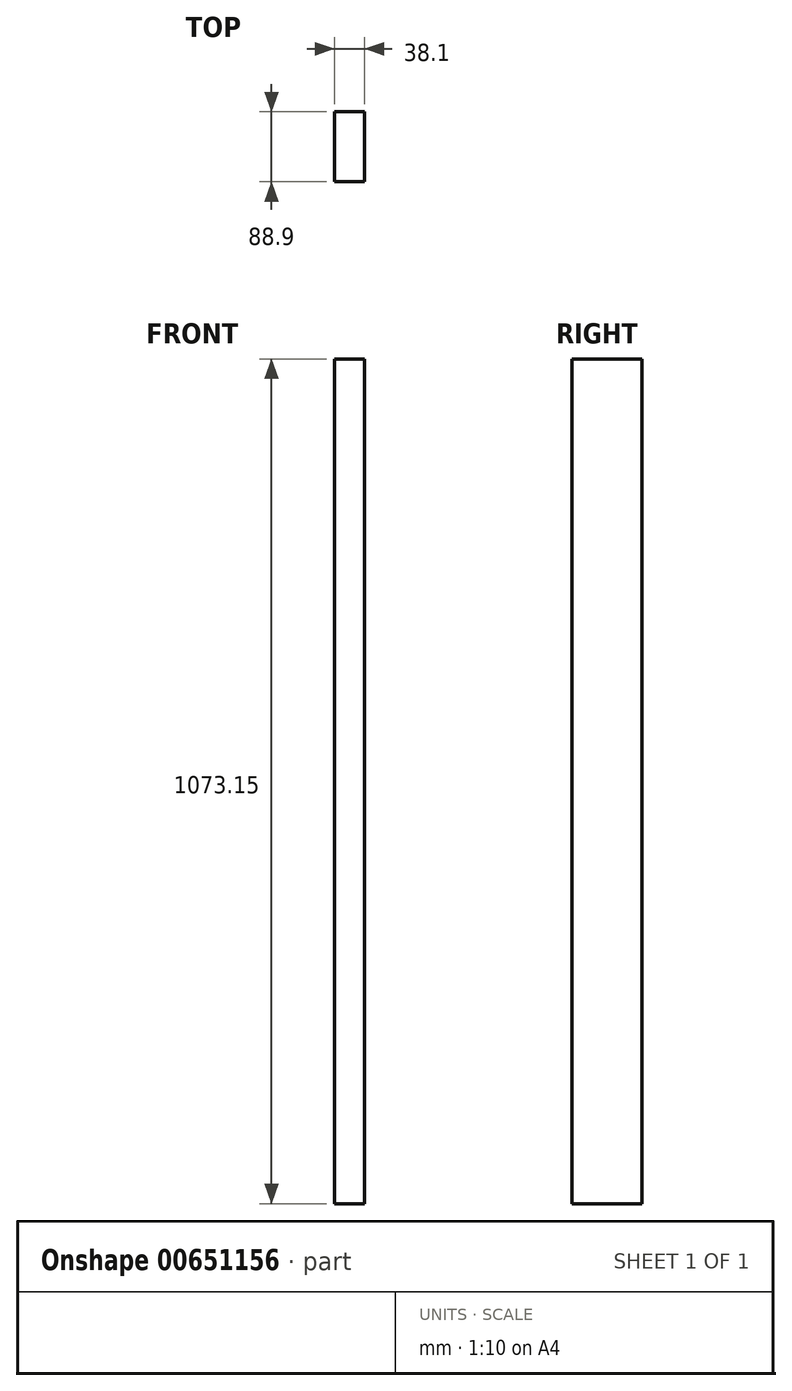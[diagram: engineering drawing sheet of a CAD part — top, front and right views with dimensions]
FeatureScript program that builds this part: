
annotation { "Feature Type Name" : "Feature", "Feature Type Description" : "" }
export const myFeature = defineFeature(function(context is Context, id is Id, definition is map)
    precondition{}
    {
        {
            var Q0;
            Q0=qCreatedBy(makeId("Top.planeOp"),FACE);
            var sketch = newSketch(context, id + "F0", { "sketchPlane" : qUnion([Q0])});
            skLineSegment(sketch, "E0.bottom", {"start": v(19.05, -44.45) * mm, "end": v(-19.05, -44.45) * mm});
            skLineSegment(sketch, "E0.top", {"start": v(19.05, 44.45) * mm, "end": v(-19.05, 44.45) * mm});
            skLineSegment(sketch, "E0.left", {"start": v(19.05, -44.45) * mm, "end": v(19.05, 44.45) * mm});
            skLineSegment(sketch, "E0.right", {"start": v(-19.05, -44.45) * mm, "end": v(-19.05, 44.45) * mm});
            skPoint(sketch, "E0.middle", {"position": v(0, 0) * mm});
            skSolve(sketch);
        }
        {
            var Q0;
            Q0 = qSketchRegion(id + "F0", true);
            var Q1;
            Q1=makeQuery(id+"F0.imprint","IMPRINT",FACE,{"disambiguationData":[TD([[makeQuery(id+"F0.imprint","IMPRINT",EDGE,{"derivedFrom":sQuery(id+"F0.wireOp",EDGE,"c484430e-5b11-4d19-9ad6-bfa51f2c2b4a.bottom")}),1.0]])]});
            extrude(context, id + "F1", {"entities" : qUnion([Q0, Q1]), "depth" : 1073.15 * mm, "offsetDistance" : 25.4 * mm});
        }
    });
